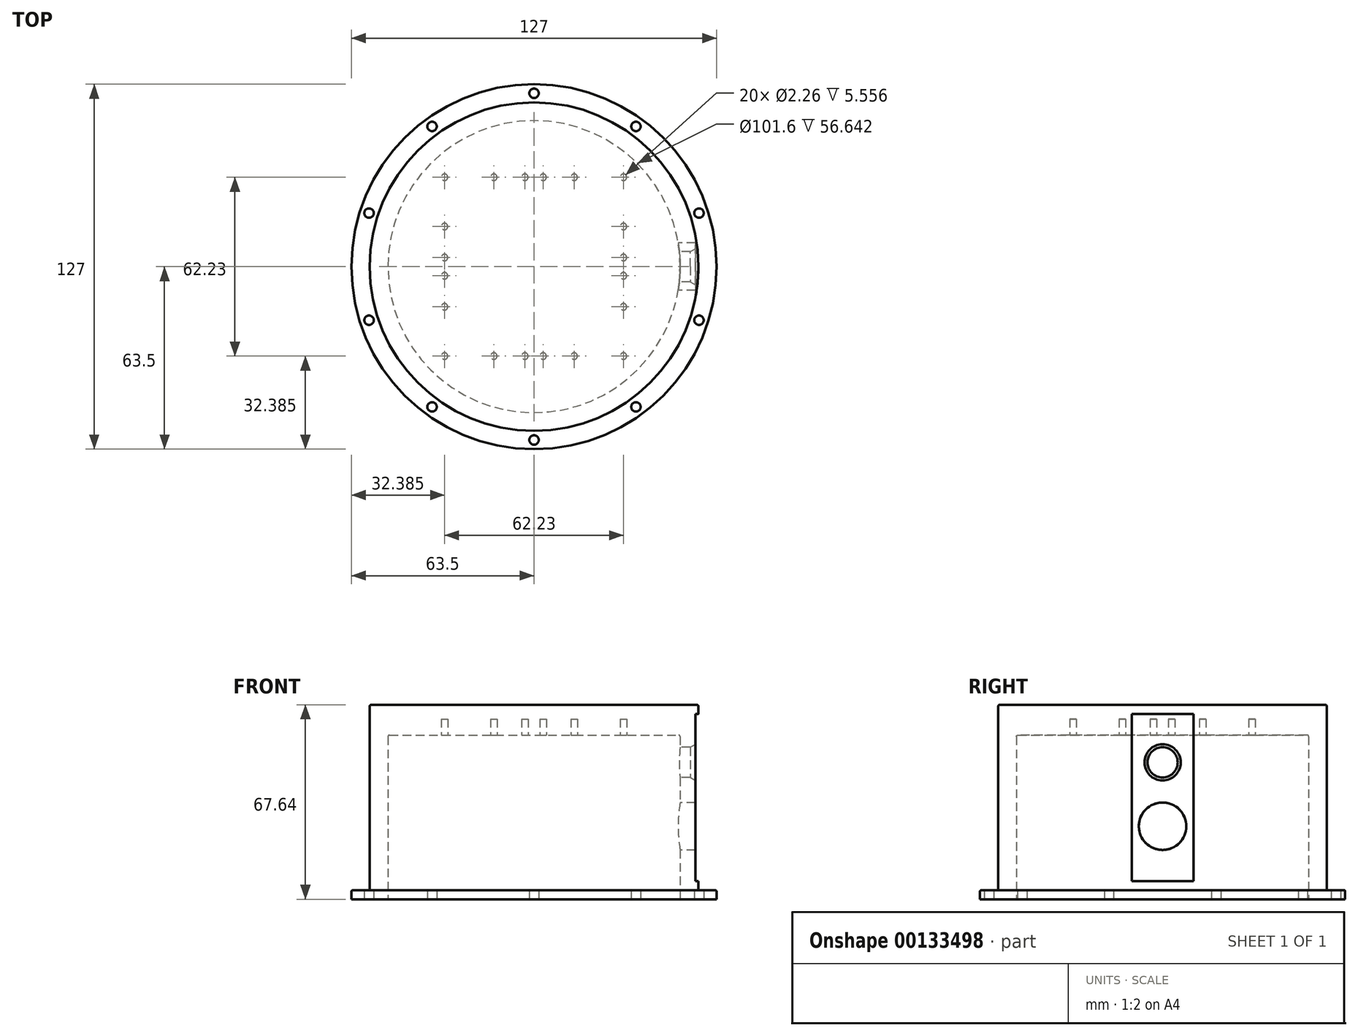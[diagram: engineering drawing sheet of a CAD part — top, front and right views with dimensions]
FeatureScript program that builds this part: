
annotation { "Feature Type Name" : "Feature", "Feature Type Description" : "" }
export const myFeature = defineFeature(function(context is Context, id is Id, definition is map)
    precondition{}
    {
        {
            var Q0;
            Q0=qCreatedBy(makeId("Top.planeOp"),FACE);
            var sketch = newSketch(context, id + "F0", { "sketchPlane" : qUnion([Q0])});
            skCircle(sketch, "E0", {"center": v(0, 0) * mm, "radius": 63.5 * mm});
            skSolve(sketch);
        }
        {
            var Q0;
            Q0=qSketchRegion(id+"F0",true);
            extrude(context, id + "F1", {"entities" : qUnion([Q0]), "depth" : 3.17 * mm});
        }
        {
            var Q0;
            Q0=qCreatedBy(makeId("Top.planeOp"),FACE);
            var sketch = newSketch(context, id + "F2", { "sketchPlane" : qUnion([Q0])});
            skCircle(sketch, "E1", {"center": v(0, 0) * mm, "radius": 57.15 * mm});
            skSolve(sketch);
        }
        {
            var Q0;
            Q0=qSketchRegion(id+"F2",true);
            extrude(context, id + "F3", {"entities" : qUnion([Q0]), "operationType" : NewBodyOperationType.ADD, "depth" : 67.64 * mm});
        }
        {
            var Q0;
            Q0=makeQuery(id+"F1.opExtrude","CAP_FACE",FACE,{"disambiguationData":[OSD([sQuery(id+"F0.wireOp",EDGE,"E0")])],"isStart":true});
            var sketch = newSketch(context, id + "F4", { "sketchPlane" : qUnion([Q0])});
            skCircle(sketch, "E2", {"center": v(0, 0) * mm, "radius": 50.8 * mm});
            skSolve(sketch);
        }
        {
            var Q0;
            Q0=qSketchRegion(id+"F4",true);
            extrude(context, id + "F5", {"entities" : qUnion([Q0]), "operationType" : NewBodyOperationType.REMOVE, "oppositeDirection" : true, "depth" : 57.15 * mm});
        }
        {
            var Q0;
            Q0=makeQuery(id+"F1.opExtrude","CAP_FACE",FACE,{"disambiguationData":[OSD([sQuery(id+"F0.wireOp",EDGE,"E0")])],"isStart":true});
            var sketch = newSketch(context, id + "F6", { "sketchPlane" : qUnion([Q0])});
            skCircle(sketch, "E3", {"center": v(0, -60.33) * mm, "radius": 1.64 * mm});
            skCircle(sketch, "E4.1.0", {"center": v(35.46, -48.8) * mm, "radius": 1.64 * mm});
            skCircle(sketch, "E4.2.0", {"center": v(57.37, -18.64) * mm, "radius": 1.64 * mm});
            skCircle(sketch, "E4.3.0", {"center": v(57.37, 18.64) * mm, "radius": 1.64 * mm});
            skCircle(sketch, "E4.4.0", {"center": v(35.46, 48.8) * mm, "radius": 1.64 * mm});
            skCircle(sketch, "E4.5.0", {"center": v(0, 60.33) * mm, "radius": 1.64 * mm});
            skCircle(sketch, "E4.6.0", {"center": v(-35.46, 48.8) * mm, "radius": 1.64 * mm});
            skCircle(sketch, "E4.7.0", {"center": v(-57.37, 18.64) * mm, "radius": 1.64 * mm});
            skCircle(sketch, "E4.8.0", {"center": v(-57.37, -18.64) * mm, "radius": 1.64 * mm});
            skCircle(sketch, "E4.9.0", {"center": v(-35.46, -48.8) * mm, "radius": 1.64 * mm});
            skPoint(sketch, "E4.center", {"position": v(0, 0) * mm});
            skSolve(sketch);
        }
        {
            var Q0;
            Q0=qSketchRegion(id+"F6",true);
            extrude(context, id + "F7", {"entities" : qUnion([Q0]), "operationType" : NewBodyOperationType.REMOVE, "endBound" : BoundingType.UP_TO_NEXT, "oppositeDirection" : true, "depth" : 25.4 * mm});
        }
        {
            var Q0;
            Q0=makeQuery(id+"F5.boolean.opBoolean","COPY",FACE,{"derivedFrom":makeQuery(id+"F5.opExtrude","CAP_FACE",FACE,{"disambiguationData":[OSD([sQuery(id+"F4.wireOp",EDGE,"E2")])],"isStart":false})});
            var sketch = newSketch(context, id + "F8", { "sketchPlane" : qUnion([Q0])});
            skLineSegment(sketch, "E5.bottom", {"start": v(-31.12, 31.11) * mm, "end": v(31.12, 31.12) * mm, "construction": true});
            skLineSegment(sketch, "E5.top", {"start": v(-31.12, -31.12) * mm, "end": v(31.11, -31.11) * mm, "construction": true});
            skLineSegment(sketch, "E5.left", {"start": v(-31.11, 31.12) * mm, "end": v(-31.12, -31.12) * mm, "construction": true});
            skLineSegment(sketch, "E5.right", {"start": v(31.12, 31.12) * mm, "end": v(31.11, -31.12) * mm, "construction": true});
            skPoint(sketch, "E5.middle", {"position": v(0, 0) * mm});
            skCircle(sketch, "E6", {"center": v(31.11, -31.12) * mm, "radius": 1.13 * mm});
            skCircle(sketch, "E7", {"center": v(-31.12, -31.12) * mm, "radius": 1.13 * mm});
            skCircle(sketch, "E8", {"center": v(-31.12, 31.12) * mm, "radius": 1.13 * mm});
            skCircle(sketch, "E9", {"center": v(31.12, 31.12) * mm, "radius": 1.13 * mm});
            skCircle(sketch, "E10", {"center": v(3.18, 31.12) * mm, "radius": 1.13 * mm});
            skCircle(sketch, "E11", {"center": v(-3.17, 31.12) * mm, "radius": 1.13 * mm});
            skCircle(sketch, "E12", {"center": v(-31.12, 3.17) * mm, "radius": 1.13 * mm});
            skCircle(sketch, "E13", {"center": v(31.12, 3.18) * mm, "radius": 1.13 * mm});
            skCircle(sketch, "E14", {"center": v(31.12, -3.17) * mm, "radius": 1.13 * mm});
            skCircle(sketch, "E15", {"center": v(3.18, -31.12) * mm, "radius": 1.13 * mm});
            skCircle(sketch, "E16", {"center": v(-3.17, -31.12) * mm, "radius": 1.13 * mm});
            skCircle(sketch, "E17", {"center": v(-31.12, -3.18) * mm, "radius": 1.13 * mm});
            skLineSegment(sketch, "E18", {"start": v(3.18, -31.12) * mm, "end": v(3.18, 31.12) * mm, "construction": true});
            skLineSegment(sketch, "E19", {"start": v(-3.17, -31.12) * mm, "end": v(-3.17, 31.12) * mm, "construction": true});
            skLineSegment(sketch, "E20", {"start": v(31.12, 3.18) * mm, "end": v(-31.12, 3.17) * mm, "construction": true});
            skLineSegment(sketch, "E21", {"start": v(31.12, -3.17) * mm, "end": v(-31.12, -3.18) * mm, "construction": true});
            skCircle(sketch, "E22", {"center": v(31.12, -13.97) * mm, "radius": 1.13 * mm});
            skCircle(sketch, "E23", {"center": v(31.12, 13.97) * mm, "radius": 1.13 * mm});
            skCircle(sketch, "E24", {"center": v(-31.12, -13.97) * mm, "radius": 1.13 * mm});
            skCircle(sketch, "E25", {"center": v(-31.12, 13.97) * mm, "radius": 1.13 * mm});
            skCircle(sketch, "E26", {"center": v(-13.97, 31.12) * mm, "radius": 1.13 * mm});
            skCircle(sketch, "E27", {"center": v(13.97, 31.12) * mm, "radius": 1.13 * mm});
            skCircle(sketch, "E28", {"center": v(13.97, -31.12) * mm, "radius": 1.13 * mm});
            skCircle(sketch, "E29", {"center": v(-13.97, -31.12) * mm, "radius": 1.13 * mm});
            skLineSegment(sketch, "E30", {"start": v(13.97, -31.12) * mm, "end": v(13.97, 31.12) * mm, "construction": true});
            skLineSegment(sketch, "E31", {"start": v(-13.97, -31.12) * mm, "end": v(-13.97, 31.12) * mm, "construction": true});
            skLineSegment(sketch, "E32", {"start": v(-31.12, 13.97) * mm, "end": v(31.12, 13.97) * mm, "construction": true});
            skLineSegment(sketch, "E33", {"start": v(31.12, -13.97) * mm, "end": v(-31.11, -13.97) * mm, "construction": true});
            skLineSegment(sketch, "E34", {"start": v(31.12, 13.97) * mm, "end": v(-31.12, -13.97) * mm, "construction": true});
            skLineSegment(sketch, "E35", {"start": v(13.97, -31.12) * mm, "end": v(-13.97, 31.12) * mm, "construction": true});
            skSolve(sketch);
        }
        {
            var Q0;
            Q0=qSketchRegion(id+"F8",true);
            extrude(context, id + "F9", {"entities" : qUnion([Q0]), "operationType" : NewBodyOperationType.REMOVE, "oppositeDirection" : true, "depth" : 5.56 * mm});
        }
        {
            var Q0;
            Q0=qCreatedBy(makeId("Right.planeOp"),FACE);
            var sketch = newSketch(context, id + "F10", { "sketchPlane" : qUnion([Q0])});
            skCircle(sketch, "E36", {"center": v(0, 25.4) * mm, "radius": 8.25 * mm});
            skCircle(sketch, "E37", {"center": v(0, 47.63) * mm, "radius": 5.25 * mm});
            skSolve(sketch);
        }
        {
            var Q0;
            Q0=qSketchRegion(id+"F10",true);
            var Q1;
            Q1=makeQuery(id+"F3.opExtrude","SWEPT_FACE",FACE,{"disambiguationData":[OSD([sQuery(id+"F2.wireOp",EDGE,"E1")])]});
            extrude(context, id + "F11", {"entities" : qUnion([Q0]), "operationType" : NewBodyOperationType.REMOVE, "endBound" : BoundingType.UP_TO_SURFACE, "endBoundEntityFace" : qUnion([Q1]), "depth" : 25.4 * mm});
        }
        {
            var Q0;
            Q0=makeQuery(id+"F3.opExtrude","CAP_EDGE",EDGE,{"disambiguationData":[OSD([sQuery(id+"F2.wireOp",EDGE,"E1")])],"isStart":false});
            var Q1;
            Q1=makeQuery(id+"F1.opExtrude","CAP_EDGE",EDGE,{"disambiguationData":[OSD([sQuery(id+"F0.wireOp",EDGE,"E0")])],"isStart":false});
            var Q2;
            Q2=makeQuery(id+"F3.boolean.opBoolean","INTERSECT",EDGE,{"derivedFrom":[makeQuery(id+"F1.opExtrude","CAP_FACE",FACE,{"disambiguationData":[OSD([sQuery(id+"F0.wireOp",EDGE,"E0")])],"isStart":false}),makeQuery(id+"F3.opExtrude","SWEPT_FACE",FACE,{"disambiguationData":[OSD([sQuery(id+"F2.wireOp",EDGE,"E1")])]})]});
            var Q3;
            Q3=makeQuery(id+"F5.boolean.opBoolean","COPY",EDGE,{"derivedFrom":makeQuery(id+"F5.opExtrude","CAP_EDGE",EDGE,{"disambiguationData":[OSD([sQuery(id+"F4.wireOp",EDGE,"E2")])],"isStart":false})});
            fillet(context, id + "F12", {"entities" : qUnion([Q0, Q1, Q2, Q3]), "radius" : 0.5 * mm, "tangentPropagation" : true, "allowEdgeOverflow" : false});
        }
        {
            var Q0;
            Q0=qCreatedBy(makeId("Right.planeOp"),FACE);
            cPlane(context, id + "F13", {"entities" : qUnion([Q0]), "cplaneType" : CPlaneType.OFFSET, "offset" : 57.15 * mm, "width" : 152.4 * mm, "height" : 152.4 * mm});
        }
        {
            var Q0;
            Q0=qCreatedBy(id+"F13.planeOp",FACE);
            var sketch = newSketch(context, id + "F14", { "sketchPlane" : qUnion([Q0])});
            skLineSegment(sketch, "E38.bottom", {"start": v(13.33, 6.35) * mm, "end": v(-13.34, 6.35) * mm});
            skLineSegment(sketch, "E38.top", {"start": v(13.33, 64.47) * mm, "end": v(-13.34, 64.47) * mm});
            skLineSegment(sketch, "E38.left", {"start": v(13.33, 6.35) * mm, "end": v(13.33, 64.47) * mm});
            skLineSegment(sketch, "E38.right", {"start": v(-13.34, 6.35) * mm, "end": v(-13.34, 64.47) * mm});
            skPoint(sketch, "E38.middle", {"position": v(0, 35.4) * mm});
            skSolve(sketch);
        }
        {
            var Q0;
            Q0 = qSketchRegion(id + "F14", true);
            var Q1;
            Q1=makeQuery(id+"F1.opExtrude","SWEPT_BODY",BODY,{"disambiguationData":[OSD([sQuery(id+"F0.wireOp",EDGE,"E0")])]});
            extrude(context, id + "F15", {"entities" : qUnion([Q0]), "operationType" : NewBodyOperationType.REMOVE, "oppositeDirection" : true, "endBoundEntityBody" : qUnion([Q1]), "depth" : 1.02 * mm});
        }
        {
            var Q0;
            Q0=makeQuery(id+"F15.boolean.opBoolean","INTERSECT",EDGE,{"derivedFrom":[makeQuery(id+"F11.boolean.opBoolean","COPY",FACE,{"derivedFrom":makeQuery(id+"F11.opExtrude","SWEPT_FACE",FACE,{"disambiguationData":[OSD([sQuery(id+"F10.wireOp",EDGE,"E37")])]})}),makeQuery(id+"F15.opExtrude","CAP_FACE",FACE,{"disambiguationData":[OSD([sQuery(id+"F14.wireOp",EDGE,"E38.bottom"),sQuery(id+"F14.wireOp",EDGE,"E38.top"),sQuery(id+"F14.wireOp",EDGE,"E38.left"),sQuery(id+"F14.wireOp",EDGE,"E38.right")])],"isStart":false})]});
            chamfer(context, id + "F16", {"entities" : qUnion([Q0]), "chamferType" : ChamferType.OFFSET_ANGLE, "width" : 1.05 * mm, "oppositeDirection" : true, "angle" : 60 * degree});
        }
    });
